# Revit family: Diffuser-Carnes-Square_Rectangular-Neck-SKSM
name_source: partatom
category: Duct Accessories
revit_build: Autodesk Revit MEP 2014 (Build: 20130308_1515(x64)
units: mm (PartAtom-declared; Revit-internal decimal feet)

## types (28) — shared parameters
C = 2 1/16"
Default Elevation = 0"
Description = Aluminum Square and Rectangular Diffusers
Flow = 0 CFM
Manufacturer = CARNES COMPANY
Model = SKSM
Revit Object Download Link = http://library.smartbim.com
Subcatagory = Air Distribution
Supply Connector = Yes
URL = http://www.carnes.com
Unit = Metal - Carnes - Aluminum

## per-type parameters (varying)
| type | A | B |
| SKSM-6Inx6In | 6" | 6" |
| SKSM-6Inx9In | 6" | 9" |
| SKSM-6Inx12In | 6" | 12" |
| SKSM-6Inx15In | 6" | 15" |
| SKSM-6Inx18In | 6" | 18" |
| SKSM-6Inx21In | 6" | 21" |
| SKSM-6Inx24In | 6" | 24" |
| SKSM-9Inx9In | 9" | 9" |
| SKSM-9Inx12In | 9" | 12" |
| SKSM-9Inx15In | 9" | 15" |
| SKSM-9Inx18In | 9" | 18" |
| SKSM-9Inx21In | 9" | 21" |
| SKSM-9Inx24In | 9" | 24" |
| SKSM-12Inx12In | 12" | 12" |
| SKSM-12Inx15In | 12" | 15" |
| SKSM-12Inx18In | 12" | 18" |
| SKSM-12Inx21In | 12" | 21" |
| SKSM-12Inx24In | 12" | 24" |
| SKSM-15Inx15In | 15" | 15" |
| SKSM-15Inx18In | 15" | 18" |
| SKSM-15Inx21In | 15" | 21" |
| SKSM-15Inx24In | 15" | 24" |
| SKSM-18Inx18In | 18" | 18" |
| SKSM-18Inx21In | 18" | 21" |
| SKSM-18Inx24In | 18" | 24" |
| SKSM-21Inx21In | 21" | 21" |
| SKSM-21Inx24In | 21" | 24" |
| SKSM-24Inx24In | 24" | 24" |

## geometry (parser evidence)
native form markers: Blend x4, Sweep x3
no freeform markers — native parametric forms only
